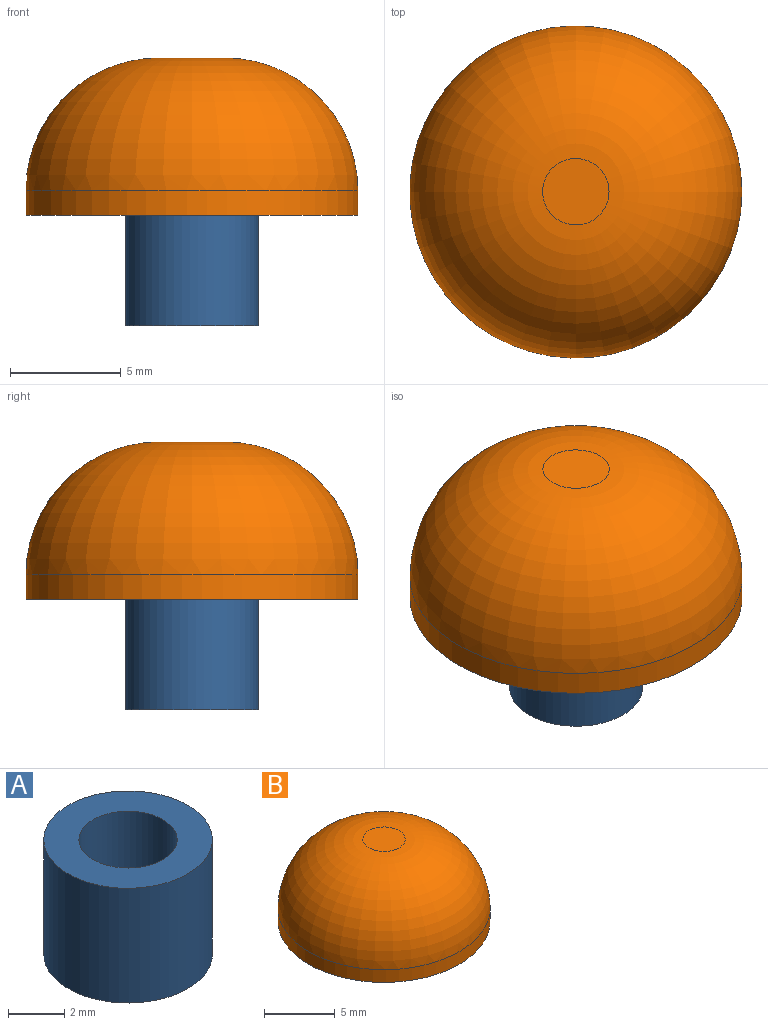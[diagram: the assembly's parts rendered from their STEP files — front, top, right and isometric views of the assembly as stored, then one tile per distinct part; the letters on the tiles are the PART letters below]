
ASSEMBLY  parts=2 mates=1
PART A: 4 faces, bbox 6x6x5 mm
  f0: cylinder r=1.75mm len=5mm, axis (0,0,-1), area 55mm2, adj f2,f3
  f1: cylinder r=3mm len=6mm, axis (0,0,-1), area 94.2mm2, adj f2,f3
  f2: plane 6x6mm, normal (0,0,1), area 18.7mm2, adj f0,f1
  f3: plane 6x6mm, normal (0,0,-1), area 18.7mm2, adj f0,f1
PART B: 6 faces, bbox 15x15x7.1 mm
  f0: cylinder r=7.5mm len=15mm, axis (0,0,-1), area 51.8mm2, adj f2,f5
  f1: plane 3x3mm, normal (0,0,1), area 7.1mm2, adj f5
  f2: plane 15x15mm, normal (0,0,-1), area 167.1mm2, adj f0,f3
  f3: cylinder r=1.75mm len=4mm, axis (0,0,-1), area 44mm2, adj f2,f4
  f4: plane 3.5x3.5mm, normal (0,0,-1), area 9.6mm2, adj f3
  f5: torus R=1.5mm, axis (0,0,1), area 315mm2, adj f0,f1
PLACE A rot(axis=(1,0,0),180deg) t=(-2.27,2.84,2.68)mm
PLACE B t=(-2.27,2.84,2.68)mm
MATE fastened A.f1 <-> B.f0  axis (0,0,1) through (-2.27,2.84,2.68)mm
